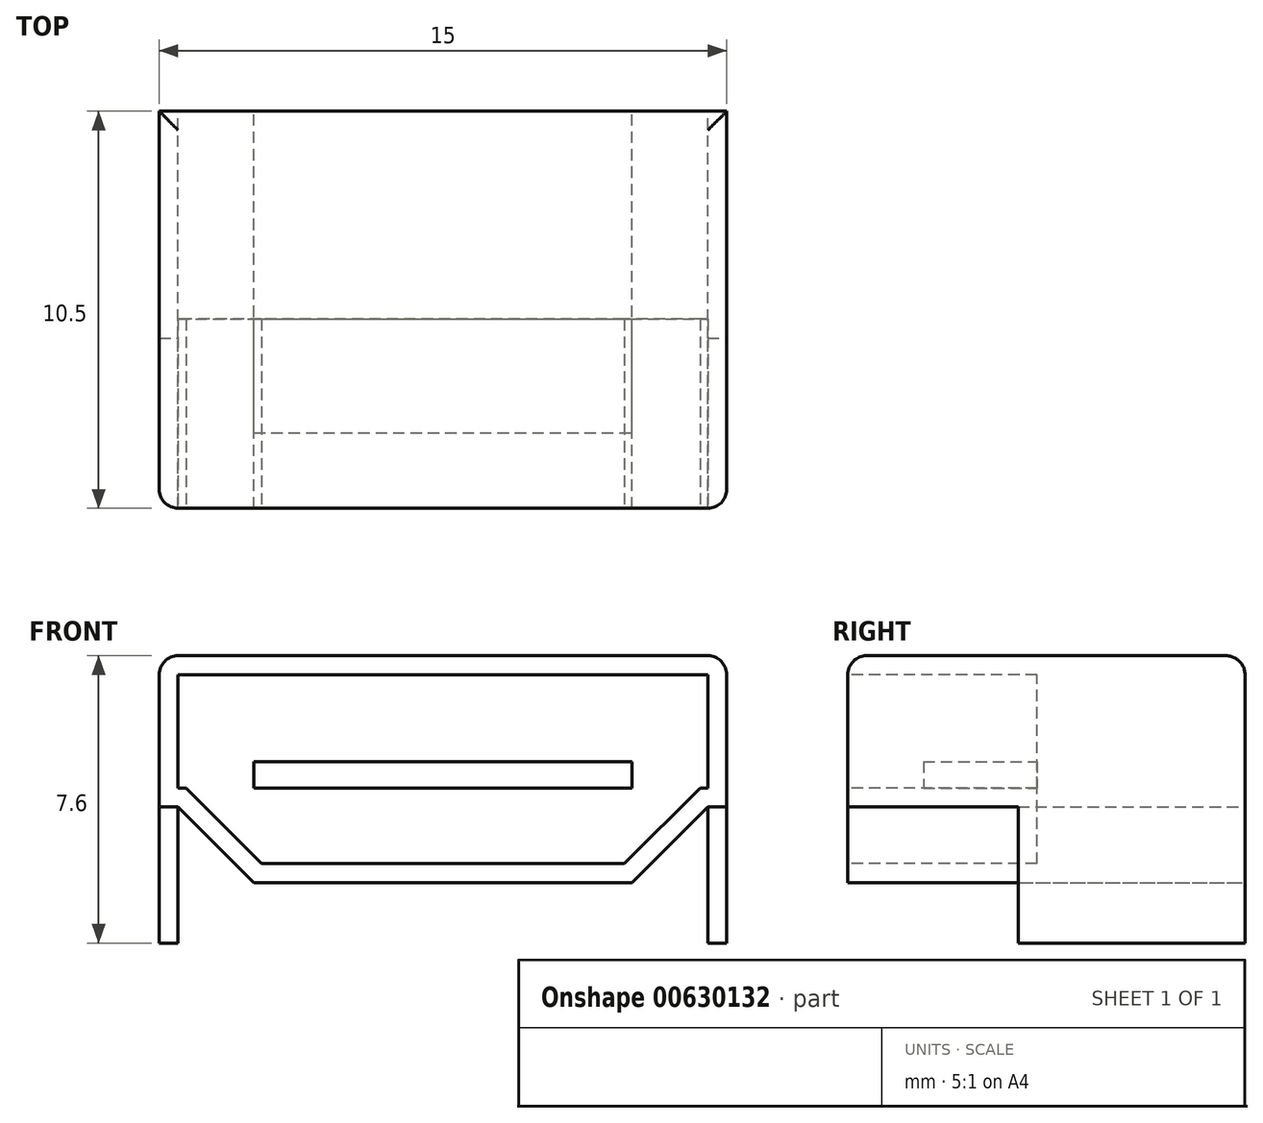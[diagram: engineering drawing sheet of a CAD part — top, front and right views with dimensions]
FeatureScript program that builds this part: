
annotation { "Feature Type Name" : "Feature", "Feature Type Description" : "" }
export const myFeature = defineFeature(function(context is Context, id is Id, definition is map)
    precondition{}
    {
        {
            var Q0;
            Q0=qCreatedBy(makeId("Front.planeOp"),FACE);
            var sketch = newSketch(context, id + "F0", { "sketchPlane" : qUnion([Q0])});
            skLineSegment(sketch, "E0.bottom", {"start": v(0, 0) * mm, "end": v(15, 0) * mm, "construction": true});
            skLineSegment(sketch, "E0.top", {"start": v(0, 6) * mm, "end": v(15, 6) * mm, "construction": true});
            skLineSegment(sketch, "E0.left", {"start": v(0, 0) * mm, "end": v(0, 6) * mm, "construction": true});
            skLineSegment(sketch, "E0.right", {"start": v(15, 0) * mm, "end": v(15, 6) * mm, "construction": true});
            skLineSegment(sketch, "E1", {"start": v(0, 6) * mm, "end": v(15, 6) * mm});
            skLineSegment(sketch, "E2", {"start": v(12.5, 0) * mm, "end": v(2.5, 0) * mm});
            skLineSegment(sketch, "E3", {"start": v(0, 2) * mm, "end": v(0, 6) * mm});
            skLineSegment(sketch, "E4", {"start": v(0, 2) * mm, "end": v(0.5, 2) * mm});
            skLineSegment(sketch, "E5", {"start": v(0.5, 2) * mm, "end": v(2.5, 0) * mm});
            skLineSegment(sketch, "E6", {"start": v(15, 2) * mm, "end": v(15, 2) * mm});
            skLineSegment(sketch, "E7", {"start": v(15, 2) * mm, "end": v(14.5, 2) * mm});
            skLineSegment(sketch, "E8", {"start": v(14.5, 2) * mm, "end": v(12.5, 0) * mm});
            skLineSegment(sketch, "E9", {"start": v(15, 6) * mm, "end": v(15, 2) * mm});
            skSolve(sketch);
        }
        {
            var Q0;
            Q0=qSketchRegion(id+"F0",true);
            extrude(context, id + "F1", {"entities" : qUnion([Q0]), "depth" : 10.5 * mm});
        }
        {
            var Q0;
            Q0=makeQuery(id+"F1.opExtrude","CAP_FACE",FACE,{"disambiguationData":[OSD([sQuery(id+"F0.wireOp",EDGE,"E1"),sQuery(id+"F0.wireOp",EDGE,"E2"),sQuery(id+"F0.wireOp",EDGE,"E3"),sQuery(id+"F0.wireOp",EDGE,"E4"),sQuery(id+"F0.wireOp",EDGE,"E5"),sQuery(id+"F0.wireOp",EDGE,"E7"),sQuery(id+"F0.wireOp",EDGE,"E8"),sQuery(id+"F0.wireOp",EDGE,"E9")])],"isStart":false});
            var sketch = newSketch(context, id + "F2", { "sketchPlane" : qUnion([Q0])});
            skLineSegment(sketch, "E10", {"start": v(0.5, 5.5) * mm, "end": v(14.5, 5.5) * mm});
            skLineSegment(sketch, "E11", {"start": v(14.5, 5.5) * mm, "end": v(14.5, 2.5) * mm});
            skLineSegment(sketch, "E12", {"start": v(14.5, 2.5) * mm, "end": v(14.3, 2.5) * mm});
            skLineSegment(sketch, "E13", {"start": v(14.3, 2.5) * mm, "end": v(12.3, 0.5) * mm});
            skLineSegment(sketch, "E14", {"start": v(12.3, 0.5) * mm, "end": v(2.7, 0.5) * mm});
            skLineSegment(sketch, "E15", {"start": v(2.7, 0.5) * mm, "end": v(0.7, 2.5) * mm});
            skLineSegment(sketch, "E16", {"start": v(0.7, 2.5) * mm, "end": v(0.5, 2.5) * mm});
            skLineSegment(sketch, "E17", {"start": v(0.5, 2.5) * mm, "end": v(0.5, 5.5) * mm});
            skSolve(sketch);
        }
        {
            var Q0;
            Q0=qSketchRegion(id+"F2",true);
            extrude(context, id + "F3", {"entities" : qUnion([Q0]), "operationType" : NewBodyOperationType.REMOVE, "oppositeDirection" : true, "depth" : 5 * mm});
        }
        {
            var Q0;
            Q0=makeQuery(id+"F3.boolean.opBoolean","COPY",FACE,{"derivedFrom":makeQuery(id+"F3.opExtrude","CAP_FACE",FACE,{"disambiguationData":[OSD([sQuery(id+"F2.wireOp",EDGE,"E10"),sQuery(id+"F2.wireOp",EDGE,"E11"),sQuery(id+"F2.wireOp",EDGE,"E12"),sQuery(id+"F2.wireOp",EDGE,"E13"),sQuery(id+"F2.wireOp",EDGE,"E14"),sQuery(id+"F2.wireOp",EDGE,"E15"),sQuery(id+"F2.wireOp",EDGE,"E16"),sQuery(id+"F2.wireOp",EDGE,"E17")])],"isStart":false})});
            var sketch = newSketch(context, id + "F4", { "sketchPlane" : qUnion([Q0])});
            skLineSegment(sketch, "E18.bottom", {"start": v(2.5, 3.2) * mm, "end": v(12.5, 3.2) * mm});
            skLineSegment(sketch, "E18.top", {"start": v(2.5, 2.5) * mm, "end": v(12.5, 2.5) * mm});
            skLineSegment(sketch, "E18.left", {"start": v(2.5, 3.2) * mm, "end": v(2.5, 2.5) * mm});
            skLineSegment(sketch, "E18.right", {"start": v(12.5, 3.2) * mm, "end": v(12.5, 2.5) * mm});
            skSolve(sketch);
        }
        {
            var Q0;
            Q0=qSketchRegion(id+"F4",true);
            extrude(context, id + "F5", {"entities" : qUnion([Q0]), "operationType" : NewBodyOperationType.ADD, "depth" : 3 * mm});
        }
        {
            var Q0;
            Q0=makeQuery(id+"F1.opExtrude","SWEPT_FACE",FACE,{"disambiguationData":[OSD([sQuery(id+"F0.wireOp",EDGE,"E4")])]});
            var sketch = newSketch(context, id + "F6", { "sketchPlane" : qUnion([Q0])});
            skLineSegment(sketch, "E19.bottom", {"start": v(0, 6) * mm, "end": v(0.5, 6) * mm});
            skLineSegment(sketch, "E19.top", {"start": v(0, 0) * mm, "end": v(0.5, 0) * mm});
            skLineSegment(sketch, "E19.left", {"start": v(0, 6) * mm, "end": v(0, 0) * mm});
            skLineSegment(sketch, "E19.right", {"start": v(0.5, 6) * mm, "end": v(0.5, 0) * mm});
            skLineSegment(sketch, "E20.bottom", {"start": v(14.5, 6) * mm, "end": v(15, 6) * mm});
            skLineSegment(sketch, "E20.top", {"start": v(14.5, 0) * mm, "end": v(15, 0) * mm});
            skLineSegment(sketch, "E20.left", {"start": v(14.5, 6) * mm, "end": v(14.5, 0) * mm});
            skLineSegment(sketch, "E20.right", {"start": v(15, 6) * mm, "end": v(15, 0) * mm});
            skSolve(sketch);
        }
        {
            var Q0;
            Q0=qSketchRegion(id+"F6",true);
            extrude(context, id + "F7", {"entities" : qUnion([Q0]), "operationType" : NewBodyOperationType.ADD, "depth" : 3.6 * mm});
        }
        {
            var Q0;
            Q0=makeQuery(id+"F1.opExtrude","SWEPT_EDGE",EDGE,{"disambiguationData":[OSD([sQuery(id+"F0.wireOp",EDGE,"E1"),sQuery(id+"F0.wireOp",EDGE,"E3")])]});
            var Q1;
            Q1=makeQuery(id+"F1.opExtrude","CAP_EDGE",EDGE,{"disambiguationData":[OSD([sQuery(id+"F0.wireOp",EDGE,"E1")])],"isStart":true});
            var Q2;
            Q2=makeQuery(id+"F1.opExtrude","SWEPT_EDGE",EDGE,{"disambiguationData":[OSD([sQuery(id+"F0.wireOp",EDGE,"E1"),sQuery(id+"F0.wireOp",EDGE,"E9")])]});
            var Q3;
            Q3=makeQuery(id+"F1.opExtrude","CAP_EDGE",EDGE,{"disambiguationData":[OSD([sQuery(id+"F0.wireOp",EDGE,"E1")])],"isStart":false});
            var Q4;
            Q4=makeQuery(id+"F1.opExtrude","CAP_EDGE",EDGE,{"disambiguationData":[OSD([sQuery(id+"F0.wireOp",EDGE,"E3")])],"isStart":false});
            var Q5;
            Q5=makeQuery(id+"F1.opExtrude","CAP_EDGE",EDGE,{"disambiguationData":[OSD([sQuery(id+"F0.wireOp",EDGE,"E9")])],"isStart":false});
            fillet(context, id + "F8", {"entities" : qUnion([Q0, Q1, Q2, Q3, Q4, Q5]), "radius" : 0.5 * mm, "tangentPropagation" : true, "allowEdgeOverflow" : false});
        }
    });
